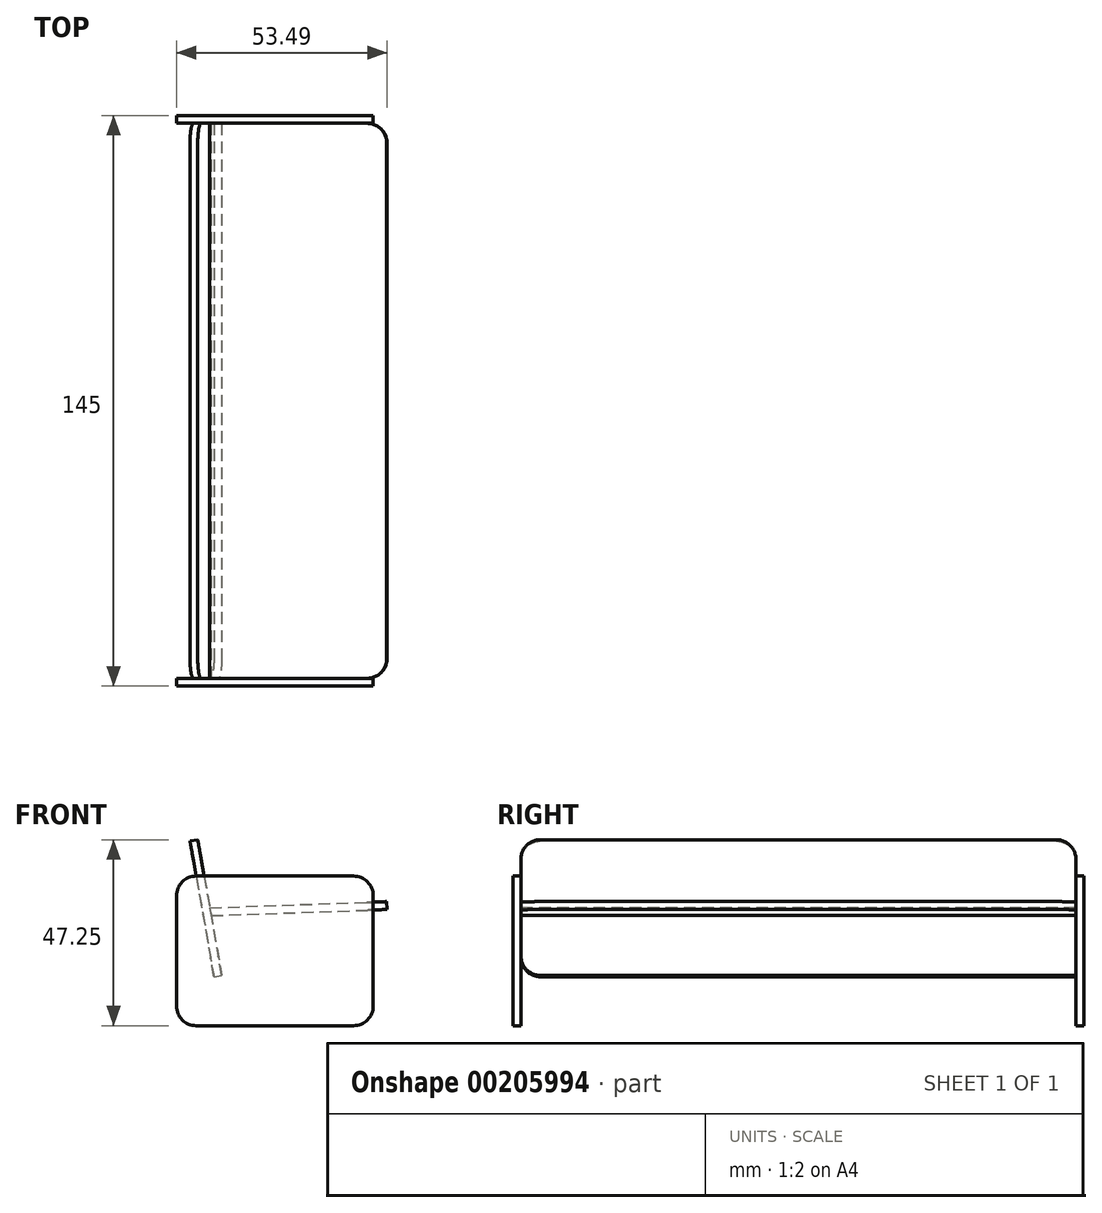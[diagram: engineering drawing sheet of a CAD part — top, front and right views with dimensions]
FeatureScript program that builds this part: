
annotation { "Feature Type Name" : "Feature", "Feature Type Description" : "" }
export const myFeature = defineFeature(function(context is Context, id is Id, definition is map)
    precondition{}
    {
        {
            var Q0;
            Q0=qCreatedBy(makeId("Front.planeOp"),FACE);
            var sketch = newSketch(context, id + "F0", { "sketchPlane" : qUnion([Q0])});
            skLineSegment(sketch, "E0.bottom", {"start": v(-25, -19) * mm, "end": v(25, -19) * mm});
            skLineSegment(sketch, "E0.top", {"start": v(-25, 19) * mm, "end": v(25, 19) * mm});
            skLineSegment(sketch, "E0.left", {"start": v(-25, -19) * mm, "end": v(-25, 19) * mm});
            skLineSegment(sketch, "E0.right", {"start": v(25, -19) * mm, "end": v(25, 19) * mm});
            skPoint(sketch, "E0.middle", {"position": v(0, 0) * mm});
            skLineSegment(sketch, "E1.bottom", {"start": v(-21.57, 27.9) * mm, "end": v(-19.6, 28.25) * mm});
            skLineSegment(sketch, "E1.top", {"start": v(-15.5, -6.57) * mm, "end": v(-13.52, -6.22) * mm});
            skLineSegment(sketch, "E1.left", {"start": v(-21.57, 27.9) * mm, "end": v(-15.5, -6.57) * mm});
            skLineSegment(sketch, "E1.right", {"start": v(-19.6, 28.25) * mm, "end": v(-13.52, -6.22) * mm});
            skLineSegment(sketch, "E2.bottom", {"start": v(-16.48, 8.95) * mm, "end": v(28.5, 10.52) * mm});
            skLineSegment(sketch, "E2.top", {"start": v(-16.55, 10.95) * mm, "end": v(28.42, 12.52) * mm});
            skLineSegment(sketch, "E2.left", {"start": v(-16.48, 8.95) * mm, "end": v(-16.55, 10.95) * mm});
            skLineSegment(sketch, "E2.right", {"start": v(28.5, 10.52) * mm, "end": v(28.42, 12.52) * mm});
            skLineSegment(sketch, "E3", {"start": v(-25, 19) * mm, "end": v(-20, 19) * mm});
            skSolve(sketch);
        }
        {
            var Q0;
            {var subQ0=sQuery(id+"F0.wireOp",EDGE,"E0.right");var subQ1=sQuery(id+"F0.wireOp",EDGE,"E0.top");var subQ2=makeQuery(id+"F0.imprint","INTERSECT",VERTEX,{"derivedFrom":[subQ1,subQ0]});Q0=makeQuery(id+"F0.imprint","IMPRINT",FACE,{"disambiguationData":[TD([[makeQuery(id+"F0.imprint","IMPRINT",EDGE,{"disambiguationData":[TD([[subQ2,1.0]])],"derivedFrom":subQ1}),-1.0]])]});}
            var Q1;
            {var subQ0=sQuery(id+"F0.wireOp",EDGE,"E2.bottom");var subQ1=sQuery(id+"F0.wireOp",EDGE,"E0.right");var subQ2=makeQuery(id+"F0.imprint","INTERSECT",VERTEX,{"derivedFrom":[subQ1,subQ0]});Q1=makeQuery(id+"F0.imprint","IMPRINT",FACE,{"disambiguationData":[TD([[makeQuery(id+"F0.imprint","IMPRINT",EDGE,{"disambiguationData":[TD([[subQ2,-1.0]])],"derivedFrom":subQ1}),1.0]])]});}
            var Q2;
            {var subQ2=sQuery(id+"F0.wireOp",EDGE,"E0.bottom");Q2=makeQuery(id+"F0.imprint","IMPRINT",FACE,{"disambiguationData":[TD([[makeQuery(id+"F0.imprint","IMPRINT",EDGE,{"derivedFrom":subQ2}),1.0]])]});}
            var Q3;
            {var subQ6=sQuery(id+"F0.wireOp",EDGE,"E1.top");Q3=makeQuery(id+"F0.imprint","IMPRINT",FACE,{"disambiguationData":[TD([[makeQuery(id+"F0.imprint","IMPRINT",EDGE,{"derivedFrom":subQ6}),1.0]])]});}
            var Q4;
            {var subQ0=sQuery(id+"F0.wireOp",EDGE,"E2.left");Q4=makeQuery(id+"F0.imprint","IMPRINT",FACE,{"disambiguationData":[TD([[makeQuery(id+"F0.imprint","IMPRINT",EDGE,{"derivedFrom":subQ0}),-1.0]])]});}
            extrude(context, id + "F1", {"entities" : qUnion([Q0, Q1, Q2, Q3, Q4]), "oppositeDirection" : true, "depth" : 2 * mm});
        }
        {
            var Q0;
            Q0=makeQuery(id+"F1.opExtrude","CAP_FACE",FACE,{"disambiguationData":[OSD([sQuery(id+"F0.wireOp",EDGE,"E0.bottom"),sQuery(id+"F0.wireOp",EDGE,"E0.top"),sQuery(id+"F0.wireOp",EDGE,"E0.left"),sQuery(id+"F0.wireOp",EDGE,"E0.right"),sQuery(id+"F0.wireOp",EDGE,"E3")])],"isStart":true});
            extrude(context, id + "F2", {"entities" : qUnion([Q0]), "operationType" : NewBodyOperationType.ADD, "oppositeDirection" : true, "depth" : 145 * mm, "hasSecondDirection" : true, "secondDirectionOppositeDirection" : true, "secondDirectionDepth" : 143 * mm});
        }
        {
            var Q0;
            {var subQ6=sQuery(id+"F0.wireOp",EDGE,"E1.top");Q0=makeQuery(id+"F0.imprint","IMPRINT",FACE,{"disambiguationData":[TD([[makeQuery(id+"F0.imprint","IMPRINT",EDGE,{"derivedFrom":subQ6}),1.0]])]});}
            var Q1;
            {var subQ5=sQuery(id+"F0.wireOp",EDGE,"E1.bottom");Q1=makeQuery(id+"F0.imprint","IMPRINT",FACE,{"disambiguationData":[TD([[makeQuery(id+"F0.imprint","IMPRINT",EDGE,{"derivedFrom":subQ5}),-1.0]])]});}
            var Q2;
            {var subQ0=sQuery(id+"F0.wireOp",EDGE,"E2.left");Q2=makeQuery(id+"F0.imprint","IMPRINT",FACE,{"disambiguationData":[TD([[makeQuery(id+"F0.imprint","IMPRINT",EDGE,{"derivedFrom":subQ0}),-1.0]])]});}
            extrude(context, id + "F3", {"entities" : qUnion([Q0, Q1, Q2]), "oppositeDirection" : true, "depth" : 143 * mm, "hasSecondDirection" : true, "secondDirectionOppositeDirection" : true, "secondDirectionDepth" : 2 * mm});
        }
        {
            var Q0;
            {var subQ0=sQuery(id+"F0.wireOp",EDGE,"E2.bottom");var subQ1=sQuery(id+"F0.wireOp",EDGE,"E0.right");var subQ2=makeQuery(id+"F0.imprint","INTERSECT",VERTEX,{"derivedFrom":[subQ1,subQ0]});Q0=makeQuery(id+"F0.imprint","IMPRINT",FACE,{"disambiguationData":[TD([[makeQuery(id+"F0.imprint","IMPRINT",EDGE,{"disambiguationData":[TD([[subQ2,-1.0]])],"derivedFrom":subQ1}),1.0]])]});}
            var Q1;
            {var subQ5=sQuery(id+"F0.wireOp",EDGE,"E2.right");Q1=makeQuery(id+"F0.imprint","IMPRINT",FACE,{"disambiguationData":[TD([[makeQuery(id+"F0.imprint","IMPRINT",EDGE,{"derivedFrom":subQ5}),1.0]])]});}
            extrude(context, id + "F4", {"entities" : qUnion([Q0, Q1]), "oppositeDirection" : true, "depth" : 143 * mm, "hasSecondDirection" : true, "secondDirectionOppositeDirection" : true, "secondDirectionDepth" : 2 * mm});
        }
        {
            var Q0;
            Q0=makeQuery(id+"F3.opExtrude","CAP_EDGE",EDGE,{"disambiguationData":[OSD([sQuery(id+"F0.wireOp",EDGE,"E1.bottom")])],"isStart":true});
            var Q1;
            Q1=makeQuery(id+"F3.opExtrude","CAP_EDGE",EDGE,{"disambiguationData":[OSD([sQuery(id+"F0.wireOp",EDGE,"E1.bottom")])],"isStart":false});
            var Q2;
            Q2=makeQuery(id+"F1.opExtrude","SWEPT_EDGE",EDGE,{"disambiguationData":[OSD([sQuery(id+"F0.wireOp",EDGE,"E0.left"),sQuery(id+"F0.wireOp",EDGE,"E3")])]});
            var Q3;
            Q3=makeQuery(id+"F1.opExtrude","SWEPT_EDGE",EDGE,{"disambiguationData":[OSD([sQuery(id+"F0.wireOp",EDGE,"E0.top"),sQuery(id+"F0.wireOp",EDGE,"E0.right")])]});
            var Q4;
            Q4=makeQuery(id+"F4.opExtrude","CAP_EDGE",EDGE,{"disambiguationData":[OSD([sQuery(id+"F0.wireOp",EDGE,"E2.right")])],"isStart":true});
            var Q5;
            Q5=makeQuery(id+"F1.opExtrude","SWEPT_EDGE",EDGE,{"disambiguationData":[OSD([sQuery(id+"F0.wireOp",EDGE,"E0.bottom"),sQuery(id+"F0.wireOp",EDGE,"E0.right")])]});
            var Q6;
            Q6=makeQuery(id+"F1.opExtrude","SWEPT_EDGE",EDGE,{"disambiguationData":[OSD([sQuery(id+"F0.wireOp",EDGE,"E0.bottom"),sQuery(id+"F0.wireOp",EDGE,"E0.left")])]});
            var Q7;
            Q7=makeQuery(id+"F3.opExtrude","CAP_EDGE",EDGE,{"disambiguationData":[OSD([sQuery(id+"F0.wireOp",EDGE,"E1.top")])],"isStart":true});
            var Q8;
            Q8=makeQuery(id+"F2.opExtrude","SWEPT_EDGE",EDGE,{"disambiguationData":[OSD([sQuery(id+"F0.wireOp",EDGE,"E0.bottom"),sQuery(id+"F0.wireOp",EDGE,"E0.right")])]});
            var Q9;
            Q9=makeQuery(id+"F2.opExtrude","SWEPT_EDGE",EDGE,{"disambiguationData":[OSD([sQuery(id+"F0.wireOp",EDGE,"E0.bottom"),sQuery(id+"F0.wireOp",EDGE,"E0.left")])]});
            var Q10;
            Q10=makeQuery(id+"F2.opExtrude","SWEPT_EDGE",EDGE,{"disambiguationData":[OSD([sQuery(id+"F0.wireOp",EDGE,"E0.left"),sQuery(id+"F0.wireOp",EDGE,"E3")])]});
            var Q11;
            Q11=makeQuery(id+"F2.opExtrude","SWEPT_EDGE",EDGE,{"disambiguationData":[OSD([sQuery(id+"F0.wireOp",EDGE,"E0.top"),sQuery(id+"F0.wireOp",EDGE,"E0.right")])]});
            var Q12;
            Q12=makeQuery(id+"F4.opExtrude","CAP_EDGE",EDGE,{"disambiguationData":[OSD([sQuery(id+"F0.wireOp",EDGE,"E2.right")])],"isStart":false});
            fillet(context, id + "F5", {"entities" : qUnion([Q0, Q1, Q2, Q3, Q4, Q5, Q6, Q7, Q8, Q9, Q10, Q11, Q12]), "radius" : 5 * mm, "tangentPropagation" : true, "allowEdgeOverflow" : false});
        }
    });
